# Revit family: Wood_Lockers_Combination_Locks-Salsbury_Industries-15_41000R_Series-3_Wide_Units.rfa
name_source: partatom
category: Specialty Equipment
revit_build: Autodesk Revit 2016 (Build: 20150220_1215(x64)
units: mm (PartAtom-declared; Revit-internal decimal feet)

## family parameters
Always vertical = Yes
Cut with Voids When Loaded = No
OmniClass Number = 23.40.00.00
OmniClass Title = Equipment and Furnishings
Part Type = Normal
Room Calculation Point = No
Round Connector Dimension = Use Diameter
Shared = No
Work Plane-Based = No

## types (6) — shared parameters
Assembly Code = C1030310
Door Location D1 = Premier Locker Doors_Resettable Lock : Single Tier Door for Six Foot High Locker
Hardware = Aluminum - Salsbury Finish - Black Satin
Interior Material = Textured Melamine - Salsbury Finish - White
Manufacturer = Salsbury Industries
MasterFormat Code = 10 51 23
MasterFormat Title = Lockers
OmniClass 23 Number = 23.40.00.00
OmniClass 23 Title = Equipment and Furnishings
Primary Structure Materials = Particle Board Industrial Grade - Salsbury Finish - Plain
Secondary Structure Materials = Particle Board Industrial Grade - Salsbury Finish - Black Melamine Overlay
Sloping In-Line Filler - Left Side = Wood Locker Sloping In-Line Fillers : None
Type Comments = Premier Wood Lockers - Single Tier - with Resettable Combination Lock
URL = www.lockers.com
Unit Height = 72.000"
Version = 1.0 (01/31/24)
Width = 45.000"

## per-type parameters (varying)
| type | Base | Base Height | Depth | Description | Model | Sloping Hood Height |
| 15-41364-R | Wood Locker Bases : Base - 45" W x 24" D Lockers | 4.000" | 24.000" | 3 Wide - 6 Feet High - 24 inches Deep - with Base | 15-41364-R | 9.118" |
| 15-41364-R - Without Base | Wood Locker Bases : None | 0.000" | 24.000" | 3 Wide - 6 Feet High - 24 inches Deep - with Base | 15-41364-R - without Base | 9.118" |
| 15-41368-R | Wood Locker Bases : Base - 45" W x 18" D Lockers | 4.000" | 18.000" | 3 Wide - 6 Feet High - 18 inches Deep - with Base | 15-41368-R | 6.868" |
| 15-41368-R - Without Base | Wood Locker Bases : None | 0.000" | 18.000" | 3 Wide - 6 Feet High - 18 inches Deep - with Base | 15-41368-R - without Base | 6.868" |
| 15-41361-R | Wood Locker Bases : Base - 45" W x 21" D Lockers | 4.000" | 21.000" | 3 Wide - 6 Feet High - 21 inches Deep - with Base | 15-41361-R | 7.993" |
| 15-41361-R - Without Base | Wood Locker Bases : None | 0.000" | 21.000" | 3 Wide - 6 Feet High - 21 inches Deep - with Base | 15-41361-R - without Base | 7.993" |

## geometry (parser evidence)
native form markers: Sweep x40
no freeform markers — native parametric forms only
